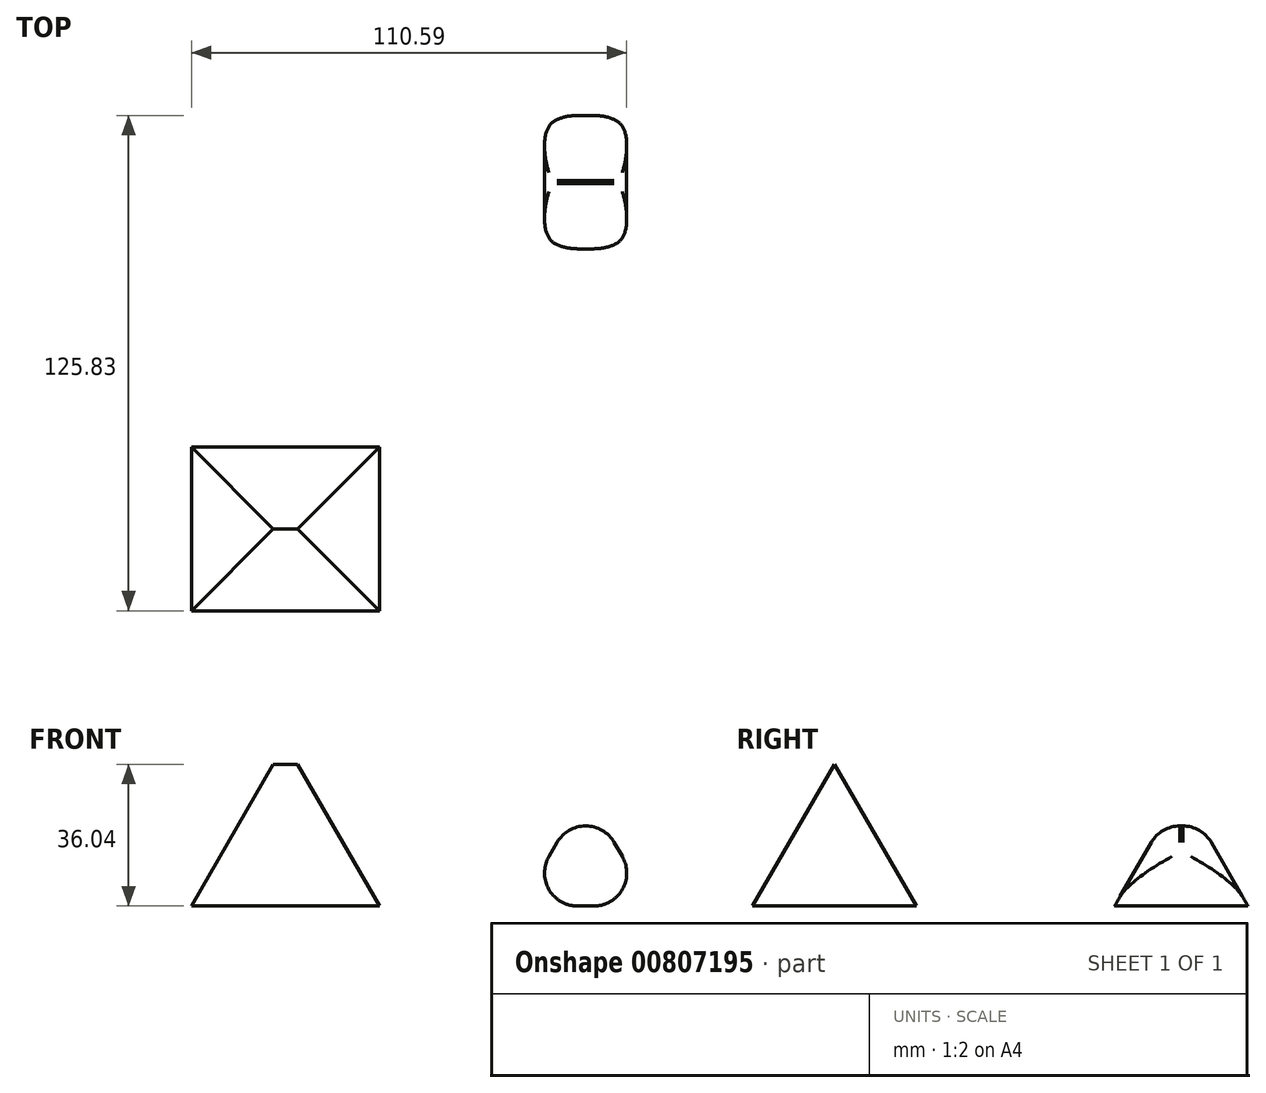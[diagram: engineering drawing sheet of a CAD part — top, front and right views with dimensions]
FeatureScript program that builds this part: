
annotation { "Feature Type Name" : "Feature", "Feature Type Description" : "" }
export const myFeature = defineFeature(function(context is Context, id is Id, definition is map)
    precondition{}
    {
        {
            var Q0;
            Q0=qCreatedBy(makeId("Top.planeOp"),FACE);
            var sketch = newSketch(context, id + "F0", { "sketchPlane" : qUnion([Q0])});
            skLineSegment(sketch, "E0.bottom", {"start": v(-59.57, -66.23) * mm, "end": v(-11.78, -66.23) * mm});
            skLineSegment(sketch, "E0.top", {"start": v(-59.57, -24.61) * mm, "end": v(-11.78, -24.61) * mm});
            skLineSegment(sketch, "E0.left", {"start": v(-59.57, -66.23) * mm, "end": v(-59.57, -24.61) * mm});
            skLineSegment(sketch, "E0.right", {"start": v(-11.78, -66.23) * mm, "end": v(-11.78, -24.61) * mm});
            skLineSegment(sketch, "E1.bottom", {"start": v(57.16, 59.6) * mm, "end": v(24, 59.6) * mm});
            skLineSegment(sketch, "E1.top", {"start": v(57.16, 25.72) * mm, "end": v(24, 25.72) * mm});
            skLineSegment(sketch, "E1.left", {"start": v(57.16, 59.6) * mm, "end": v(57.16, 25.72) * mm});
            skLineSegment(sketch, "E1.right", {"start": v(24, 59.6) * mm, "end": v(24, 25.72) * mm});
            skSolve(sketch);
        }
        {
            var Q0;
            Q0 = qSketchRegion(id + "F0", true);
            extrude(context, id + "F1", {"entities" : qUnion([Q0]), "depth" : 67.56 * mm, "offsetDistance" : 25.4 * mm, "hasDraft" : true, "draftAngle" : 30 * degree, "draftPullDirection" : true});
        }
        {
            var Q0;
            Q0=makeQuery(id+"F1.opExtrude","SWEPT_FACE",FACE,{"disambiguationData":[OSD([sQuery(id+"F0.wireOp",EDGE,"E1.left")])]});
            var Q1;
            Q1=makeQuery(id+"F1.opExtrude","SWEPT_FACE",FACE,{"disambiguationData":[OSD([sQuery(id+"F0.wireOp",EDGE,"E1.right")])]});
            fillet(context, id + "F2", {"entities" : qUnion([Q0, Q1]), "radius" : 8.38 * mm, "tangentPropagation" : true, "allowEdgeOverflow" : false});
        }
    });
